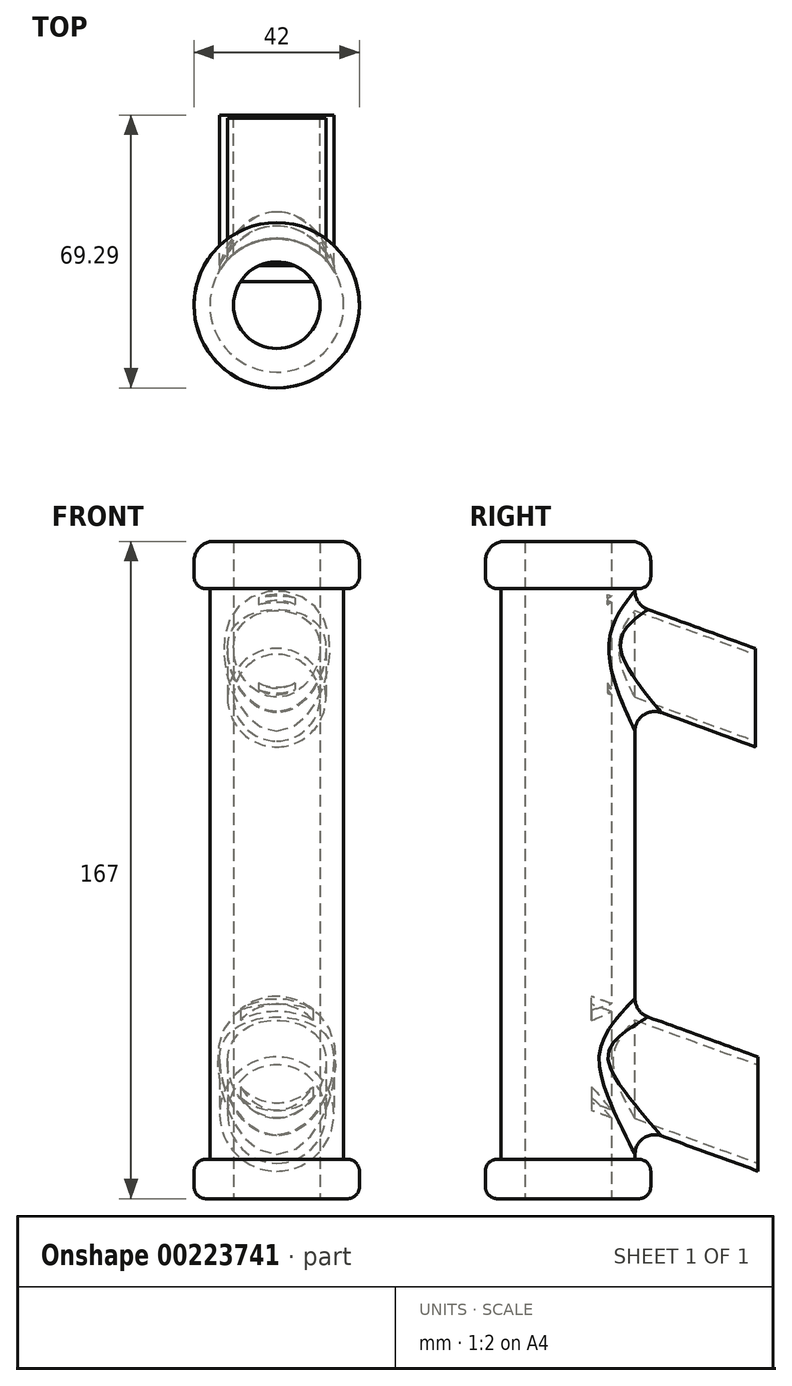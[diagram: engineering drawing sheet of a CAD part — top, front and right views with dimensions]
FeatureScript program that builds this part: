
annotation { "Feature Type Name" : "Feature", "Feature Type Description" : "" }
export const myFeature = defineFeature(function(context is Context, id is Id, definition is map)
    precondition{}
    {
        {
            var Q0;
            Q0=qCreatedBy(makeId("Top.planeOp"),FACE);
            var sketch = newSketch(context, id + "F0", { "sketchPlane" : qUnion([Q0])});
            skCircle(sketch, "E0", {"center": v(0, 0) * mm, "radius": 11 * mm});
            skCircle(sketch, "E1", {"center": v(0, 0) * mm, "radius": 17 * mm});
            skSolve(sketch);
        }
        {
            var Q0;
            Q0=qCreatedBy(makeId("Top.planeOp"),FACE);
            var sketch = newSketch(context, id + "F1", { "sketchPlane" : qUnion([Q0])});
            skCircle(sketch, "E2", {"center": v(0, 0) * mm, "radius": 21 * mm});
            skCircle(sketch, "E3", {"center": v(0, 0) * mm, "radius": 11 * mm});
            skSolve(sketch);
        }
        {
            var Q0;
            Q0=makeQuery(id+"F1.imprint","IMPRINT",FACE,{"disambiguationData":[TD([[makeQuery(id+"F1.imprint","IMPRINT",EDGE,{"derivedFrom":sQuery(id+"F1.wireOp",EDGE,"E2")}),1.0]])]});
            extrude(context, id + "F2", {"entities" : qUnion([Q0]), "depth" : 12 * mm});
        }
        {
            var Q0;
            Q0=makeQuery(id+"F2.opExtrude","CAP_EDGE",EDGE,{"disambiguationData":[OSD([sQuery(id+"F1.wireOp",EDGE,"E2")])],"isStart":false});
            fillet(context, id + "F3", {"entities" : qUnion([Q0]), "radius" : 5 * mm, "tangentPropagation" : true, "allowEdgeOverflow" : false});
        }
        {
            var Q0;
            Q0=makeQuery(id+"F0.imprint","IMPRINT",FACE,{"disambiguationData":[TD([[makeQuery(id+"F0.imprint","IMPRINT",EDGE,{"derivedFrom":sQuery(id+"F0.wireOp",EDGE,"E0")}),-1.0]])]});
            extrude(context, id + "F4", {"entities" : qUnion([Q0]), "operationType" : NewBodyOperationType.ADD, "oppositeDirection" : true, "depth" : 145 * mm});
        }
        {
            var Q0;
            Q0=makeQuery(id+"F4.opExtrude","CAP_FACE",FACE,{"disambiguationData":[OSD([sQuery(id+"F0.wireOp",EDGE,"E0"),sQuery(id+"F0.wireOp",EDGE,"E1")])],"isStart":false});
            var sketch = newSketch(context, id + "F5", { "sketchPlane" : qUnion([Q0])});
            skCircle(sketch, "E4", {"center": v(0, 0) * mm, "radius": 11 * mm});
            skCircle(sketch, "E5", {"center": v(0, 0) * mm, "radius": 21 * mm});
            skSolve(sketch);
        }
        {
            var Q0;
            Q0=makeQuery(id+"F5.imprint","IMPRINT",FACE,{"disambiguationData":[TD([[makeQuery(id+"F5.imprint","IMPRINT",EDGE,{"derivedFrom":sQuery(id+"F5.wireOp",EDGE,"E5")}),1.0]])]});
            extrude(context, id + "F6", {"entities" : qUnion([Q0]), "depth" : 10 * mm});
        }
        {
            var Q0;
            Q0=makeQuery(id+"F6.opExtrude","CAP_EDGE",EDGE,{"disambiguationData":[OSD([sQuery(id+"F5.wireOp",EDGE,"E5")])],"isStart":false});
            fillet(context, id + "F7", {"entities" : qUnion([Q0]), "radius" : 5 * mm, "tangentPropagation" : true, "allowEdgeOverflow" : false});
        }
        {
            var Q0;
            Q0=makeQuery(id+"F2.opExtrude","CAP_EDGE",EDGE,{"disambiguationData":[OSD([sQuery(id+"F1.wireOp",EDGE,"E2")])],"isStart":true});
            var Q1;
            Q1=makeQuery(id+"F6.opExtrude","CAP_EDGE",EDGE,{"disambiguationData":[OSD([sQuery(id+"F5.wireOp",EDGE,"E5")])],"isStart":true});
            fillet(context, id + "F8", {"entities" : qUnion([Q0, Q1]), "radius" : 3 * mm, "tangentPropagation" : true, "allowEdgeOverflow" : false});
        }
        {
            var Q0;
            Q0=makeQuery(id+"F6.opExtrude","SWEPT_BODY",BODY,{"disambiguationData":[OSD([sQuery(id+"F0.wireOp",EDGE,"E1"),sQuery(id+"F5.wireOp",EDGE,"E5")])]});
            var Q1;
            Q1=makeQuery(id+"F2.opExtrude","SWEPT_BODY",BODY,{"disambiguationData":[OSD([sQuery(id+"F1.wireOp",EDGE,"E2"),sQuery(id+"F1.wireOp",EDGE,"E3")])]});
            transform(context, id + "F9", {"entities" : qUnion([Q0, Q1]), "transformType" : TransformType.TRANSLATION_3D, "dx" : 0 * mm, "dy" : 0 * mm, "dz" : 0 * mm, "makeCopy" : false});
        }
        {
            var Q0;
            Q0=makeQuery(id+"F6.opExtrude","SWEPT_BODY",BODY,{"disambiguationData":[OSD([sQuery(id+"F0.wireOp",EDGE,"E1"),sQuery(id+"F5.wireOp",EDGE,"E5")])]});
            deleteBodies(context, id + "F10", {"entities" : qUnion([Q0])});
        }
        {
            var Q0;
            Q0=makeQuery(id+"F4.opExtrude","CAP_FACE",FACE,{"disambiguationData":[OSD([sQuery(id+"F0.wireOp",EDGE,"E0"),sQuery(id+"F0.wireOp",EDGE,"E1")])],"isStart":false});
            var sketch = newSketch(context, id + "F11", { "sketchPlane" : qUnion([Q0])});
            skCircle(sketch, "E6", {"center": v(0, 0) * mm, "radius": 11 * mm});
            skCircle(sketch, "E7", {"center": v(0, 0) * mm, "radius": 21 * mm});
            skSolve(sketch);
        }
        {
            var Q0;
            Q0=qSketchRegion(id+"F11",true);
            extrude(context, id + "F12", {"entities" : qUnion([Q0]), "operationType" : NewBodyOperationType.ADD, "depth" : 10 * mm});
        }
        {
            var Q0;
            Q0=makeQuery(id+"F12.opExtrude","CAP_EDGE",EDGE,{"disambiguationData":[OSD([sQuery(id+"F11.wireOp",EDGE,"E7")])],"isStart":true});
            var Q1;
            Q1=makeQuery(id+"F12.opExtrude","CAP_EDGE",EDGE,{"disambiguationData":[OSD([sQuery(id+"F11.wireOp",EDGE,"E7")])],"isStart":false});
            fillet(context, id + "F13", {"entities" : qUnion([Q0, Q1]), "radius" : 3 * mm, "tangentPropagation" : true, "allowEdgeOverflow" : false});
        }
        {
            var Q0;
            Q0=qCreatedBy(makeId("Front.planeOp"),FACE);
            cPlane(context, id + "F14", {"entities" : qUnion([Q0]), "cplaneType" : CPlaneType.OFFSET, "offset" : 10 * mm, "oppositeDirection" : true, "width" : 150 * mm, "height" : 150 * mm});
        }
        {
            var Q0;
            Q0=qCreatedBy(id+"F14.planeOp",FACE);
            var sketch = newSketch(context, id + "F15", { "sketchPlane" : qUnion([Q0])});
            skCircle(sketch, "E8", {"center": v(0, -14.04) * mm, "radius": 12.5 * mm});
            skCircle(sketch, "E9", {"center": v(0, -14.04) * mm, "radius": 11 * mm});
            skSolve(sketch);
        }
        {
            var Q0;
            Q0=qCreatedBy(makeId("Right.planeOp"),FACE);
            var sketch = newSketch(context, id + "F16", { "sketchPlane" : qUnion([Q0])});
            skLineSegment(sketch, "E10", {"start": v(33.75, -22.99) * mm, "end": v(71.34, -36.67) * mm});
            skSolve(sketch);
        }
        {
            var Q0;
            Q0=makeQuery(id+"F15.imprint","IMPRINT",FACE,{"disambiguationData":[TD([[makeQuery(id+"F15.imprint","IMPRINT",EDGE,{"derivedFrom":sQuery(id+"F15.wireOp",EDGE,"E8")}),1.0]])]});
            var Q1;
            Q1=sQuery(id+"F16.wireOp",EDGE,"E10");
            sweep(context, id + "F17", {"profiles" : qUnion([Q0]), "path" : qUnion([Q1])});
        }
        {
            var Q0;
            Q0=makeQuery(id+"F2.opExtrude","SWEPT_BODY",BODY,{"disambiguationData":[OSD([sQuery(id+"F1.wireOp",EDGE,"E2"),sQuery(id+"F1.wireOp",EDGE,"E3")])]});
            var Q1;
            Q1=makeQuery(id+"F17.opSweep","SWEPT_BODY",BODY,{"disambiguationData":[OSD([sQuery(id+"F15.wireOp",EDGE,"E8"),sQuery(id+"F16.wireOp",EDGE,"E10")])]});
            booleanBodies(context, id + "F18", {"operationType" : BooleanOperationType.UNION, "tools" : qUnion([Q0, Q1])});
        }
        {
            var Q0;
            Q0=makeQuery(id+"FTnsy99bn0V6LCi_3.opSweep","SWEPT_FACE",FACE,{"disambiguationData":[OSD([sQuery(id+"FvxowGDLgEz3hhw_3.wireOp",EDGE,"H5RKFatL-PG05-9WvE-zMDJ-it3hLgjJzGq0"),sQuery(id+"F0wyV6HheXHK4RY_3.wireOp",EDGE,"on58jkzw-FDvU-Ccj5-tRD4-fV2YOKnsHrNK")])]});
            var Q1;
            Q1=makeQuery(id+"F18.opBoolean","INTERSECT",EDGE,{"derivedFrom":[makeQuery(id+"F4.opExtrude","SWEPT_FACE",FACE,{"disambiguationData":[OSD([sQuery(id+"F0.wireOp",EDGE,"E1")])]}),makeQuery(id+"F17.opSweep","SWEPT_FACE",FACE,{"disambiguationData":[OSD([sQuery(id+"F15.wireOp",EDGE,"E8"),sQuery(id+"F16.wireOp",EDGE,"E10")])]})]});
            fillet(context, id + "F19", {"entities" : qUnion([Q0, Q1]), "radius" : 5 * mm, "tangentPropagation" : true, "allowEdgeOverflow" : false});
        }
        {
            var Q0;
            Q0=qCreatedBy(makeId("Front.planeOp"),FACE);
            cPlane(context, id + "F20", {"entities" : qUnion([Q0]), "cplaneType" : CPlaneType.OFFSET, "offset" : 6 * mm, "oppositeDirection" : true, "width" : 150 * mm, "height" : 150 * mm});
        }
        {
            var Q0;
            Q0=qCreatedBy(id+"F20.planeOp",FACE);
            var sketch = newSketch(context, id + "F21", { "sketchPlane" : qUnion([Q0])});
            skCircle(sketch, "E11", {"center": v(0, -118.12) * mm, "radius": 14.5 * mm});
            skCircle(sketch, "E12", {"center": v(0, -118.12) * mm, "radius": 12.5 * mm});
            skSolve(sketch);
        }
        {
            var Q0;
            Q0=qCreatedBy(makeId("Right.planeOp"),FACE);
            var sketch = newSketch(context, id + "F22", { "sketchPlane" : qUnion([Q0])});
            skLineSegment(sketch, "E13", {"start": v(17.76, -122.72) * mm, "end": v(60.05, -138.11) * mm});
            skSolve(sketch);
        }
        {
            var Q0;
            Q0=makeQuery(id+"F21.imprint","IMPRINT",FACE,{"disambiguationData":[TD([[makeQuery(id+"F21.imprint","IMPRINT",EDGE,{"derivedFrom":sQuery(id+"F21.wireOp",EDGE,"E11")}),1.0]])]});
            var Q1;
            Q1=sQuery(id+"F22.wireOp",EDGE,"E13");
            sweep(context, id + "F23", {"profiles" : qUnion([Q0]), "path" : qUnion([Q1])});
        }
        {
            var Q0;
            Q0=makeQuery(id+"F23.opSweep","SWEPT_BODY",BODY,{"disambiguationData":[OSD([sQuery(id+"F21.wireOp",EDGE,"E11"),sQuery(id+"F22.wireOp",EDGE,"E13")])]});
            var Q1;
            Q1=makeQuery(id+"F2.opExtrude","SWEPT_BODY",BODY,{"disambiguationData":[OSD([sQuery(id+"F1.wireOp",EDGE,"E2"),sQuery(id+"F1.wireOp",EDGE,"E3")])]});
            booleanBodies(context, id + "F24", {"operationType" : BooleanOperationType.UNION, "tools" : qUnion([Q0, Q1])});
        }
        {
            var Q0;
            Q0=makeQuery(id+"F24.opBoolean","INTERSECT",EDGE,{"derivedFrom":[makeQuery(id+"F4.opExtrude","SWEPT_FACE",FACE,{"disambiguationData":[OSD([sQuery(id+"F0.wireOp",EDGE,"E1")])]}),makeQuery(id+"F23.opSweep","SWEPT_FACE",FACE,{"disambiguationData":[OSD([sQuery(id+"F21.wireOp",EDGE,"E11"),sQuery(id+"F22.wireOp",EDGE,"E13")])]})]});
            fillet(context, id + "F25", {"entities" : qUnion([Q0]), "radius" : 5 * mm, "tangentPropagation" : true, "allowEdgeOverflow" : false});
        }
    });
